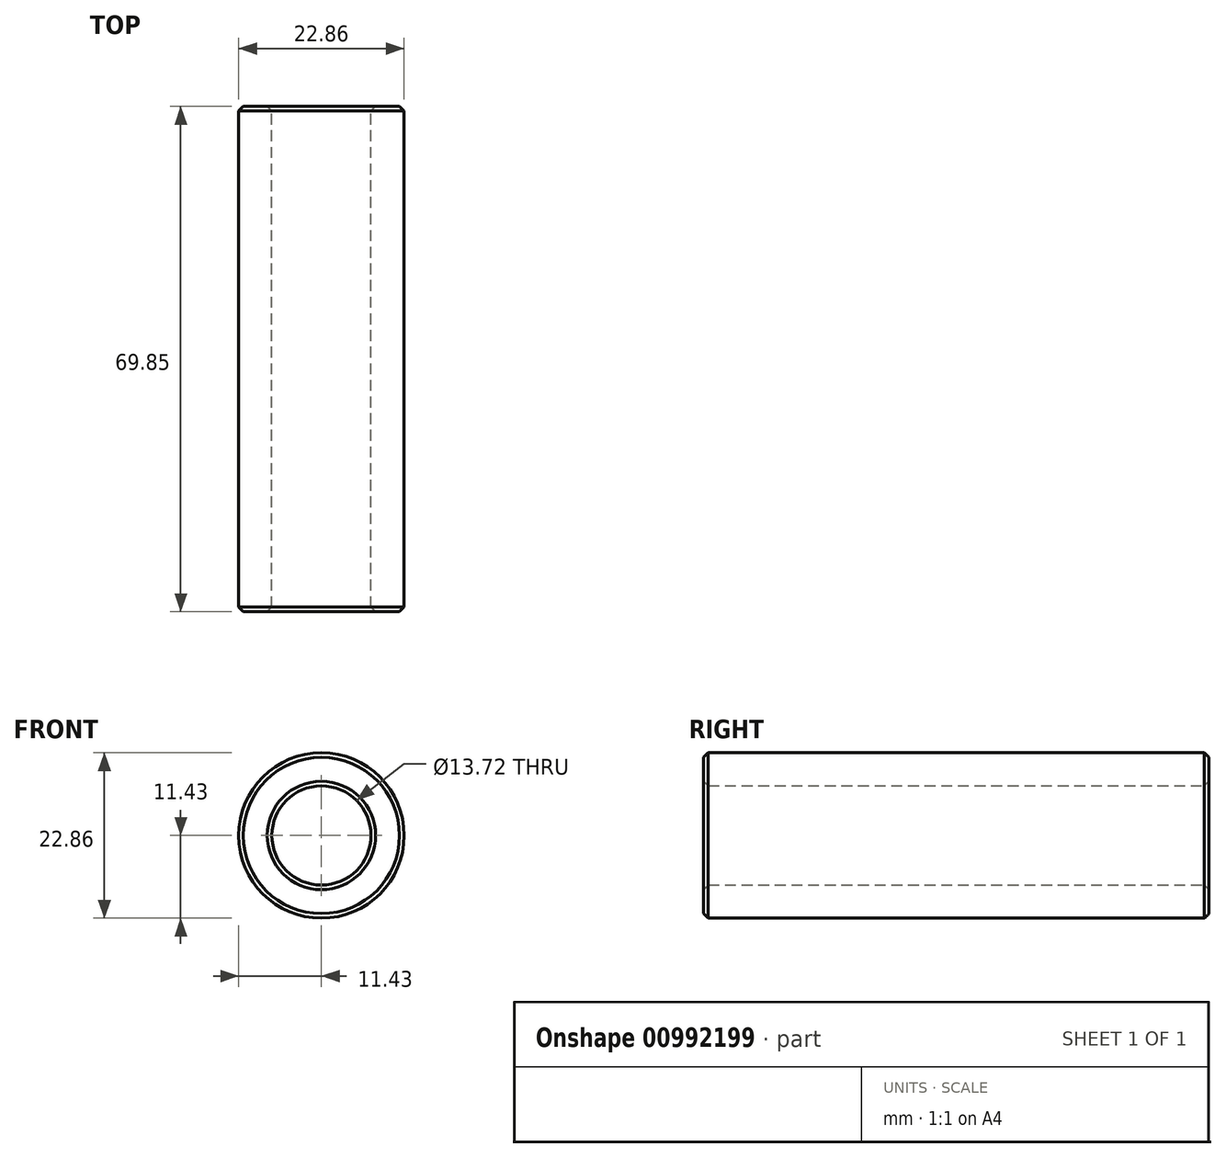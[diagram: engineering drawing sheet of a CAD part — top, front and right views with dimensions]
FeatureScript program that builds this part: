
annotation { "Feature Type Name" : "Feature", "Feature Type Description" : "" }
export const myFeature = defineFeature(function(context is Context, id is Id, definition is map)
    precondition{}
    {
        {
            var Q0;
            Q0=qCreatedBy(makeId("Front.planeOp"),FACE);
            var sketch = newSketch(context, id + "F0", { "sketchPlane" : qUnion([Q0])});
            skCircle(sketch, "E0", {"center": v(0, 0) * mm, "radius": 6.86 * mm});
            skCircle(sketch, "E1", {"center": v(0, 0) * mm, "radius": 11.43 * mm});
            skSolve(sketch);
        }
        {
            var Q0;
            Q0=makeQuery(id+"F0.imprint","IMPRINT",FACE,{"disambiguationData":[TD([[makeQuery(id+"F0.imprint","IMPRINT",EDGE,{"derivedFrom":sQuery(id+"F0.wireOp",EDGE,"E0")}),-1.0]])]});
            extrude(context, id + "F1", {"entities" : qUnion([Q0]), "depth" : 69.85 * mm, "offsetDistance" : 25.4 * mm});
        }
        {
            var Q0;
            Q0=makeQuery(id+"F1.opExtrude","CAP_EDGE",EDGE,{"disambiguationData":[OSD([sQuery(id+"F0.wireOp",EDGE,"E0")])],"isStart":false});
            var Q1;
            Q1=makeQuery(id+"F1.opExtrude","CAP_EDGE",EDGE,{"disambiguationData":[OSD([sQuery(id+"F0.wireOp",EDGE,"E1")])],"isStart":false});
            var Q2;
            Q2=makeQuery(id+"F1.opExtrude","CAP_EDGE",EDGE,{"disambiguationData":[OSD([sQuery(id+"F0.wireOp",EDGE,"E1")])],"isStart":true});
            var Q3;
            Q3=makeQuery(id+"F1.opExtrude","SWEPT_FACE",FACE,{"disambiguationData":[OSD([sQuery(id+"F0.wireOp",EDGE,"E0")])]});
            chamfer(context, id + "F2", {"entities" : qUnion([Q0, Q1, Q2, Q3]), "width" : 0.64 * mm, "tangentPropagation" : true});
        }
    });
